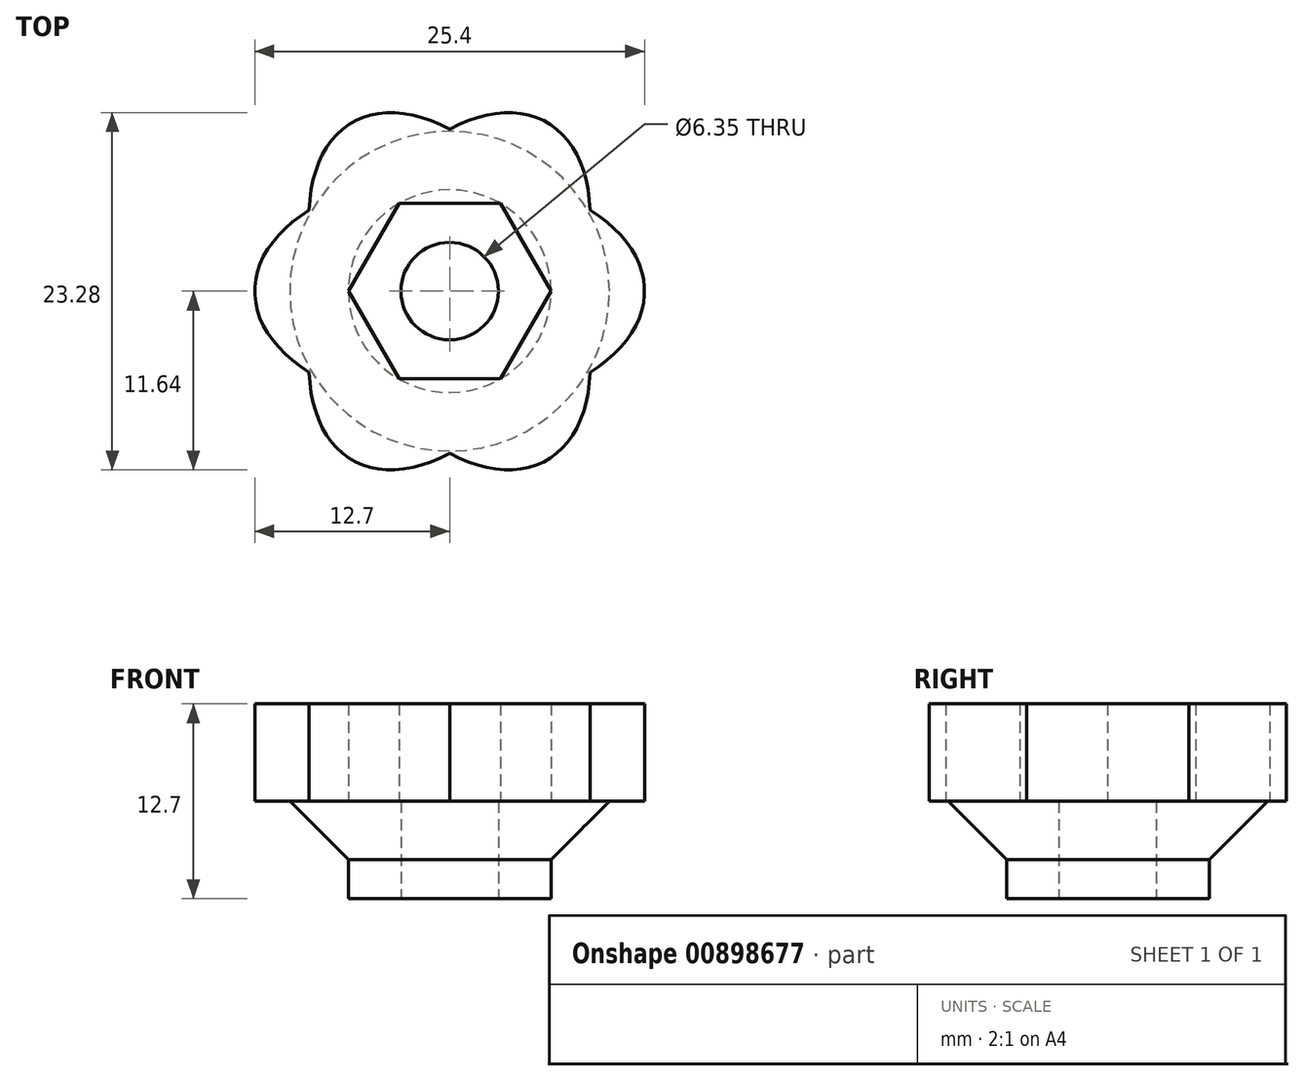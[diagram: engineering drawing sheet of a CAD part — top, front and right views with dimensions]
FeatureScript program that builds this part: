
annotation { "Feature Type Name" : "Feature", "Feature Type Description" : "" }
export const myFeature = defineFeature(function(context is Context, id is Id, definition is map)
    precondition{}
    {
        {
            var Q0;
            Q0=qCreatedBy(makeId("Top.planeOp"),FACE);
            var sketch = newSketch(context, id + "F0", { "sketchPlane" : qUnion([Q0])});
            skCircle(sketch, "E0", {"center": v(0, 0) * mm, "radius": 3.17 * mm});
            skCircle(sketch, "E1", {"center": v(0, 0) * mm, "radius": 6.6 * mm});
            skSolve(sketch);
        }
        {
            var Q0;
            Q0=qSketchRegion(id+"F0",true);
            extrude(context, id + "F1", {"entities" : qUnion([Q0]), "depth" : 2.54 * mm, "offsetDistance" : 25.4 * mm});
        }
        {
            var Q0;
            Q0=makeQuery(id+"F1.opExtrude","CAP_FACE",FACE,{"disambiguationData":[OSD([sQuery(id+"F0.wireOp",EDGE,"E0"),sQuery(id+"F0.wireOp",EDGE,"E1")])],"isStart":false});
            var sketch = newSketch(context, id + "F2", { "sketchPlane" : qUnion([Q0])});
            skCircle(sketch, "E2", {"center": v(0, 0) * mm, "radius": 6.6 * mm});
            skCircle(sketch, "E3", {"center": v(0, 0) * mm, "radius": 3.18 * mm});
            skCircle(sketch, "E4", {"center": v(0, 0) * mm, "radius": 10.41 * mm});
            skSolve(sketch);
        }
        {
            var Q0;
            Q0=qSketchRegion(id+"F2",true);
            var Q1;
            Q1=makeQuery(id+"F2.imprint","IMPRINT",FACE,{"disambiguationData":[TD([[makeQuery(id+"F2.imprint","IMPRINT",EDGE,{"derivedFrom":sQuery(id+"F2.wireOp",EDGE,"E2")}),1.0]])]});
            extrude(context, id + "F3", {"entities" : qUnion([Q0, Q1]), "operationType" : NewBodyOperationType.ADD, "depth" : 3.8 * mm, "offsetDistance" : 25.4 * mm});
        }
        {
            var Q0;
            Q0=makeQuery(id+"F3.opExtrude","CAP_EDGE",EDGE,{"disambiguationData":[OSD([sQuery(id+"F2.wireOp",EDGE,"E4")])],"isStart":true});
            chamfer(context, id + "F4", {"entities" : qUnion([Q0]), "width" : 3.8 * mm, "tangentPropagation" : true});
        }
        {
            var Q0;
            Q0=makeQuery(id+"F3.opExtrude","CAP_FACE",FACE,{"disambiguationData":[OSD([sQuery(id+"F2.wireOp",EDGE,"E3"),sQuery(id+"F2.wireOp",EDGE,"E4")])],"isStart":false});
            var sketch = newSketch(context, id + "F5", { "sketchPlane" : qUnion([Q0])});
            skEllipticalArc(sketch, "E5", {});
            skEllipticalArc(sketch, "E6.1.0", {});
            skEllipticalArc(sketch, "E6.2.0", {});
            skPoint(sketch, "E6.center", {"position": v(0, 1) * mm});
            skCircle(sketch, "E7.cCircle", {"center": v(0, 0) * mm, "radius": 5.72 * mm, "construction": true});
            skLineSegment(sketch, "E7.0", {"start": v(-3.3, 5.72) * mm, "end": v(3.3, 5.72) * mm});
            skLineSegment(sketch, "E7.1", {"start": v(3.3, 5.71) * mm, "end": v(6.6, 0) * mm});
            skLineSegment(sketch, "E7.2", {"start": v(6.6, 0) * mm, "end": v(3.3, -5.72) * mm});
            skLineSegment(sketch, "E7.3", {"start": v(3.3, -5.72) * mm, "end": v(-3.3, -5.72) * mm});
            skLineSegment(sketch, "E7.4", {"start": v(-3.3, -5.72) * mm, "end": v(-6.6, 0) * mm});
            skLineSegment(sketch, "E7.5", {"start": v(-6.6, 0) * mm, "end": v(-3.3, 5.72) * mm});
            skPoint(sketch, "E7.0.midPoint", {"position": v(0, 5.72) * mm});
            skLineSegment(sketch, "E8", {"start": v(-9.94, -4.74) * mm, "end": v(-4.95, -2.86) * mm, "construction": true});
            skLineSegment(sketch, "E9", {"start": v(9.94, -4.74) * mm, "end": v(5.16, -2.46) * mm, "construction": true});
            skLineSegment(sketch, "E10", {"start": v(0, 12.48) * mm, "end": v(0, 5.72) * mm, "construction": true});
            skEllipticalArc(sketch, "E11.trimOffspring", {});
            skEllipticalArc(sketch, "E12.trimOffspring", {});
            skEllipticalArc(sketch, "E13.trimOffspring", {});
            skLineSegment(sketch, "E14", {"start": v(0, -8.56) * mm, "end": v(0, -5.72) * mm, "construction": true});
            skLineSegment(sketch, "E15", {"start": v(-4.95, 2.86) * mm, "end": v(-8.28, 5.78) * mm, "construction": true});
            skLineSegment(sketch, "E16", {"start": v(4.95, 2.86) * mm, "end": v(8.28, 5.78) * mm, "construction": true});
            const initialGuessF5  = {"E5": [0, 0, 1, 0, 0.012700642459094524, 0.00762, 5.516997383150618, 0.7661879240289684], "E6.1.0": [0, 0, -0.5, 0.8660254037844387, 0.012700642459094524, 0.00762, 2.3754047295608247, 3.9077805776187606], "E6.2.0": [0, 0, -0.5, -0.8660254037844384, 0.012700642459094524, 0.00762, 2.375404729560825, 3.90778057761876], "E11.trimOffspring": [0, 0, -0.5, -0.8660254037844384, 0.012700642459094524, 0.00762, 5.516997383150618, 0.7661879240289691], "E12.trimOffspring": [0, 0, 1, 0, 0.012700642459094524, 0.00762, 2.375404729560824, 3.9077805776187606], "E13.trimOffspring": [0, 0, -0.5, 0.8660254037844387, 0.012700642459094524, 0.00762, 5.516997383150617, 0.7661879240289693]};
            skSetInitialGuess(sketch, initialGuessF5);
            skSolve(sketch);
        }
        {
            var Q0;
            Q0=qSketchRegion(id+"F5",true);
            extrude(context, id + "F6", {"entities" : qUnion([Q0]), "operationType" : NewBodyOperationType.ADD, "depth" : 6.35 * mm, "offsetDistance" : 25.4 * mm});
        }
    });
